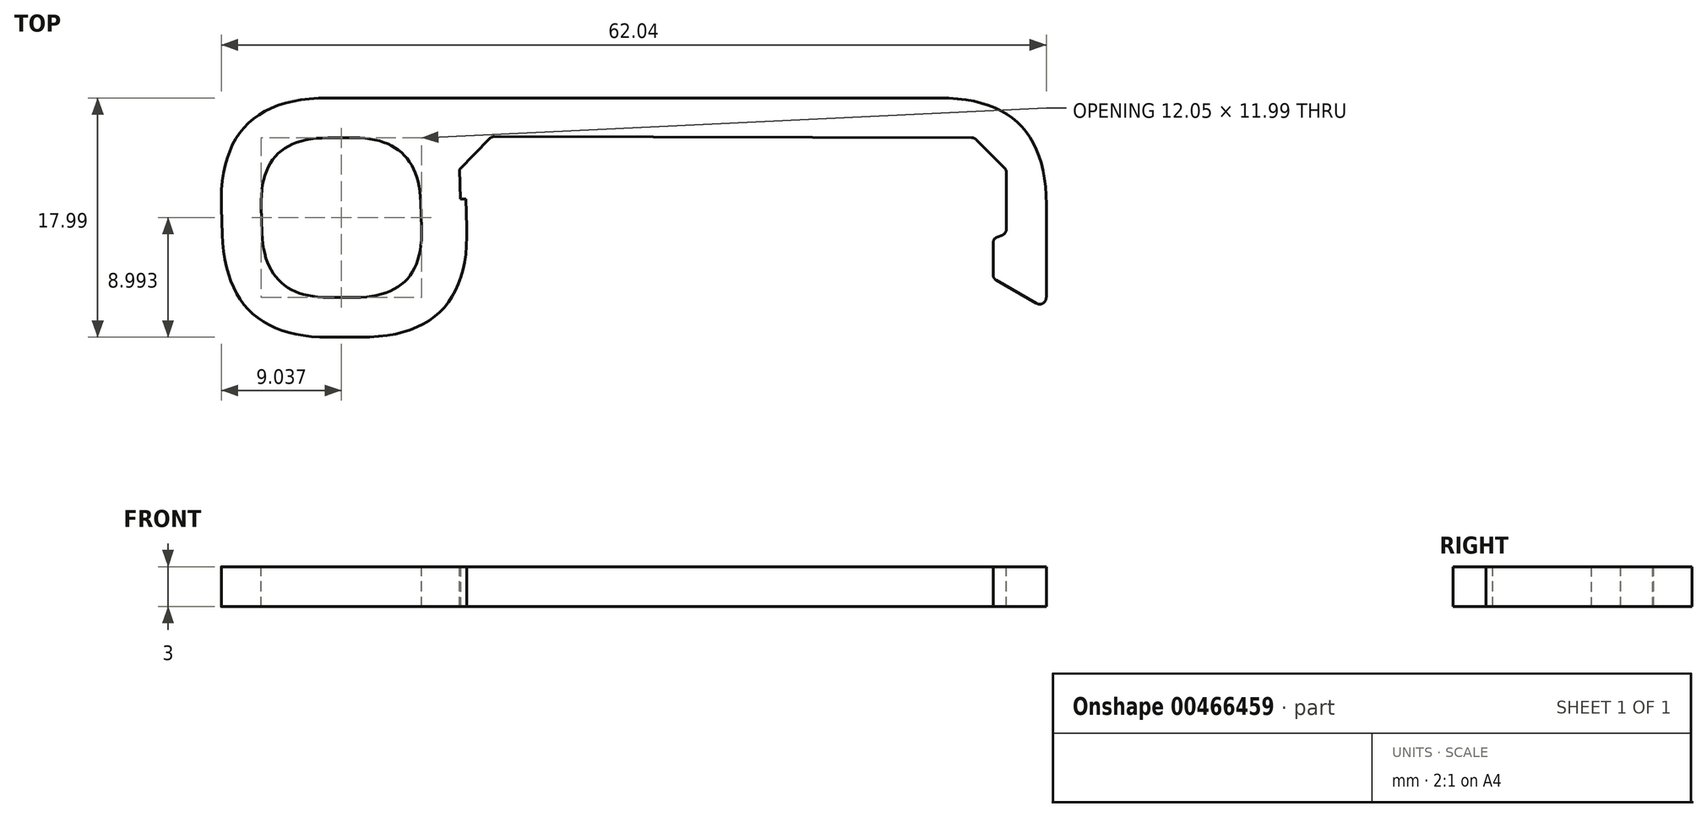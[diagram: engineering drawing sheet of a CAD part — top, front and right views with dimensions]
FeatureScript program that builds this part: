
annotation { "Feature Type Name" : "Feature", "Feature Type Description" : "" }
export const myFeature = defineFeature(function(context is Context, id is Id, definition is map)
    precondition{}
    {
        {
            var Q0;
            Q0=qCreatedBy(makeId("Top.planeOp"),FACE);
            var sketch = newSketch(context, id + "F0", { "sketchPlane" : qUnion([Q0])});
            skLineSegment(sketch, "E0", {"start": v(-3, 0) * mm, "end": v(-3, -7.2) * mm});
            skLineSegment(sketch, "E1", {"start": v(-3, -7.2) * mm, "end": v(-4, -7.56) * mm});
            skLineSegment(sketch, "E2", {"start": v(-4, -7.56) * mm, "end": v(-4, -10.56) * mm});
            skLineSegment(sketch, "E3", {"start": v(-4, -10.56) * mm, "end": v(0, -12.87) * mm});
            skLineSegment(sketch, "E4", {"start": v(0, -12.87) * mm, "end": v(0, 3) * mm});
            skLineSegment(sketch, "E5", {"start": v(0, 3) * mm, "end": v(-62.3, 3) * mm});
            skLineSegment(sketch, "E6", {"start": v(-62.3, 3) * mm, "end": v(-61.71, -15) * mm});
            skLineSegment(sketch, "E7", {"start": v(-61.71, -15) * mm, "end": v(-43.3, -15) * mm});
            skLineSegment(sketch, "E8", {"start": v(-44.2, 0.1) * mm, "end": v(-3, 0) * mm});
            skLineSegment(sketch, "E9", {"start": v(-3, 0) * mm, "end": v(0, 0) * mm, "construction": true});
            skLineSegment(sketch, "E10", {"start": v(-3, 3) * mm, "end": v(-3, 0) * mm, "construction": true});
            skLineSegment(sketch, "E11.bottom", {"start": v(-47.2, 0) * mm, "end": v(-59.2, 0) * mm});
            skLineSegment(sketch, "E11.top", {"start": v(-46.8, -12) * mm, "end": v(-58.8, -12) * mm});
            skLineSegment(sketch, "E11.left", {"start": v(-47.2, 0) * mm, "end": v(-46.8, -12) * mm});
            skLineSegment(sketch, "E11.right", {"start": v(-59.2, 0) * mm, "end": v(-58.8, -12) * mm});
            skLineSegment(sketch, "E12", {"start": v(-46.8, -12) * mm, "end": v(-46.71, -15) * mm, "construction": true});
            skLineSegment(sketch, "E13", {"start": v(-44.2, 0.1) * mm, "end": v(-44.05, -4.6) * mm});
            skLineSegment(sketch, "E14", {"start": v(-44.05, -4.6) * mm, "end": v(-43.65, -4.59) * mm});
            skLineSegment(sketch, "E15", {"start": v(-43.65, -4.59) * mm, "end": v(-43.3, -15) * mm});
            skLineSegment(sketch, "E16", {"start": v(-59.2, 0) * mm, "end": v(-62.2, -0.1) * mm, "construction": true});
            skLineSegment(sketch, "E17", {"start": v(-44.2, 0.1) * mm, "end": v(-47.2, 0) * mm, "construction": true});
            skSolve(sketch);
        }
        {
            var Q0;
            Q0 = qSketchRegion(id + "F0", true);
            extrude(context, id + "F1", {"entities" : qUnion([Q0]), "depth" : 3 * mm});
        }
        {
            var Q0;
            Q0=makeQuery(id+"F1.opExtrude","SWEPT_EDGE",EDGE,{"disambiguationData":[OSD([sQuery(id+"F0.wireOp",EDGE,"JGTh3lzA-ujIE-Ue52-w2xY-UzFVIg36bVys"),sQuery(id+"F0.wireOp",EDGE,"E8")])]});
            var Q1;
            Q1=makeQuery(id+"F1.opExtrude","SWEPT_EDGE",EDGE,{"disambiguationData":[OSD([sQuery(id+"F0.wireOp",EDGE,"E0"),sQuery(id+"F0.wireOp",EDGE,"E8")])]});
            chamfer(context, id + "F2", {"entities" : qUnion([Q0, Q1]), "width" : 2.4 * mm, "tangentPropagation" : true});
        }
        {
            var Q0;
            Q0=makeQuery(id+"F1.opExtrude","SWEPT_EDGE",EDGE,{"disambiguationData":[OSD([sQuery(id+"F0.wireOp",EDGE,"E11.bottom"),sQuery(id+"F0.wireOp",EDGE,"E11.left")])]});
            var Q1;
            Q1=makeQuery(id+"F1.opExtrude","SWEPT_EDGE",EDGE,{"disambiguationData":[OSD([sQuery(id+"F0.wireOp",EDGE,"E11.top"),sQuery(id+"F0.wireOp",EDGE,"E11.left")])]});
            var Q2;
            Q2=makeQuery(id+"F1.opExtrude","SWEPT_EDGE",EDGE,{"disambiguationData":[OSD([sQuery(id+"F0.wireOp",EDGE,"E11.top"),sQuery(id+"F0.wireOp",EDGE,"E11.right")])]});
            var Q3;
            Q3=makeQuery(id+"F1.opExtrude","SWEPT_EDGE",EDGE,{"disambiguationData":[OSD([sQuery(id+"F0.wireOp",EDGE,"E11.bottom"),sQuery(id+"F0.wireOp",EDGE,"E11.right")])]});
            fillet(context, id + "F3", {"entities" : qUnion([Q0, Q1, Q2, Q3]), "radius" : 5 * mm, "tangentPropagation" : true, "rho" : .5, "crossSection" : FilletCrossSection.CONIC, "allowEdgeOverflow" : false});
        }
        {
            var Q0;
            Q0=makeQuery(id+"F1.opExtrude","SWEPT_EDGE",EDGE,{"disambiguationData":[OSD([sQuery(id+"F0.wireOp",EDGE,"E5"),sQuery(id+"F0.wireOp",EDGE,"E6")])]});
            var Q1;
            Q1=makeQuery(id+"F1.opExtrude","SWEPT_EDGE",EDGE,{"disambiguationData":[OSD([sQuery(id+"F0.wireOp",EDGE,"E6"),sQuery(id+"F0.wireOp",EDGE,"E7")])]});
            var Q2;
            Q2=makeQuery(id+"F1.opExtrude","SWEPT_EDGE",EDGE,{"disambiguationData":[OSD([sQuery(id+"F0.wireOp",EDGE,"E7"),sQuery(id+"F0.wireOp",EDGE,"JGTh3lzA-ujIE-Ue52-w2xY-UzFVIg36bVys")])]});
            fillet(context, id + "F4", {"entities" : qUnion([Q0, Q1, Q2]), "radius" : 8 * mm, "tangentPropagation" : true, "rho" : .5, "crossSection" : FilletCrossSection.CONIC, "allowEdgeOverflow" : false});
        }
        {
            var Q0;
            Q0=makeQuery(id+"F1.opExtrude","SWEPT_EDGE",EDGE,{"disambiguationData":[OSD([sQuery(id+"F0.wireOp",EDGE,"E4"),sQuery(id+"F0.wireOp",EDGE,"E5")])]});
            fillet(context, id + "F5", {"entities" : qUnion([Q0]), "radius" : 8 * mm, "tangentPropagation" : true, "rho" : .5, "crossSection" : FilletCrossSection.CONIC, "allowEdgeOverflow" : false});
        }
        {
            var Q0;
            Q0=makeQuery(id+"F1.opExtrude","SWEPT_EDGE",EDGE,{"disambiguationData":[OSD([sQuery(id+"F0.wireOp",EDGE,"E3"),sQuery(id+"F0.wireOp",EDGE,"E4")])]});
            var Q1;
            Q1=makeQuery(id+"F1.opExtrude","SWEPT_EDGE",EDGE,{"disambiguationData":[OSD([sQuery(id+"F0.wireOp",EDGE,"E2"),sQuery(id+"F0.wireOp",EDGE,"E3")])]});
            var Q2;
            Q2=makeQuery(id+"F1.opExtrude","SWEPT_EDGE",EDGE,{"disambiguationData":[OSD([sQuery(id+"F0.wireOp",EDGE,"E1"),sQuery(id+"F0.wireOp",EDGE,"E2")])]});
            var Q3;
            Q3=makeQuery(id+"F1.opExtrude","SWEPT_EDGE",EDGE,{"disambiguationData":[OSD([sQuery(id+"F0.wireOp",EDGE,"E0"),sQuery(id+"F0.wireOp",EDGE,"E1")])]});
            var Q4;
            {var subQ0=sQuery(id+"F0.wireOp",EDGE,"E0");Q4=makeQuery(id+"F2.opChamfer","BLEND_EDGE",EDGE,{"blendedFrom":[makeQuery(id+"F1.opExtrude","SWEPT_EDGE",EDGE,{"disambiguationData":[OSD([subQ0,sQuery(id+"F0.wireOp",EDGE,"E8")])]}),makeQuery(id+"F1.opExtrude","SWEPT_FACE",FACE,{"disambiguationData":[OSD([subQ0])]})],"blendedInto":[makeQuery(id+"F1.opExtrude","SWEPT_FACE",FACE,{"disambiguationData":[OSD([subQ0])]})]});}
            var Q5;
            {var subQ0=sQuery(id+"F0.wireOp",EDGE,"E8");Q5=makeQuery(id+"F2.opChamfer","BLEND_EDGE",EDGE,{"blendedFrom":[makeQuery(id+"F1.opExtrude","SWEPT_EDGE",EDGE,{"disambiguationData":[OSD([sQuery(id+"F0.wireOp",EDGE,"E0"),subQ0])]}),makeQuery(id+"F1.opExtrude","SWEPT_FACE",FACE,{"disambiguationData":[OSD([subQ0])]})],"blendedInto":[makeQuery(id+"F1.opExtrude","SWEPT_FACE",FACE,{"disambiguationData":[OSD([subQ0])]})]});}
            var Q6;
            {var subQ0=sQuery(id+"F0.wireOp",EDGE,"E8");Q6=makeQuery(id+"F2.opChamfer","BLEND_EDGE",EDGE,{"blendedFrom":[makeQuery(id+"F1.opExtrude","SWEPT_EDGE",EDGE,{"disambiguationData":[OSD([sQuery(id+"F0.wireOp",EDGE,"JGTh3lzA-ujIE-Ue52-w2xY-UzFVIg36bVys"),subQ0])]}),makeQuery(id+"F1.opExtrude","SWEPT_FACE",FACE,{"disambiguationData":[OSD([subQ0])]})],"blendedInto":[makeQuery(id+"F1.opExtrude","SWEPT_FACE",FACE,{"disambiguationData":[OSD([subQ0])]})]});}
            var Q7;
            {var subQ0=sQuery(id+"F0.wireOp",EDGE,"JGTh3lzA-ujIE-Ue52-w2xY-UzFVIg36bVys");Q7=makeQuery(id+"F2.opChamfer","BLEND_EDGE",EDGE,{"blendedFrom":[makeQuery(id+"F1.opExtrude","SWEPT_EDGE",EDGE,{"disambiguationData":[OSD([subQ0,sQuery(id+"F0.wireOp",EDGE,"E8")])]}),makeQuery(id+"F1.opExtrude","SWEPT_FACE",FACE,{"disambiguationData":[OSD([subQ0])]})],"blendedInto":[makeQuery(id+"F1.opExtrude","SWEPT_FACE",FACE,{"disambiguationData":[OSD([subQ0])]})]});}
            fillet(context, id + "F6", {"entities" : qUnion([Q0, Q1, Q2, Q3, Q4, Q5, Q6, Q7]), "radius" : .5 * mm, "tangentPropagation" : true, "allowEdgeOverflow" : false});
        }
    });
